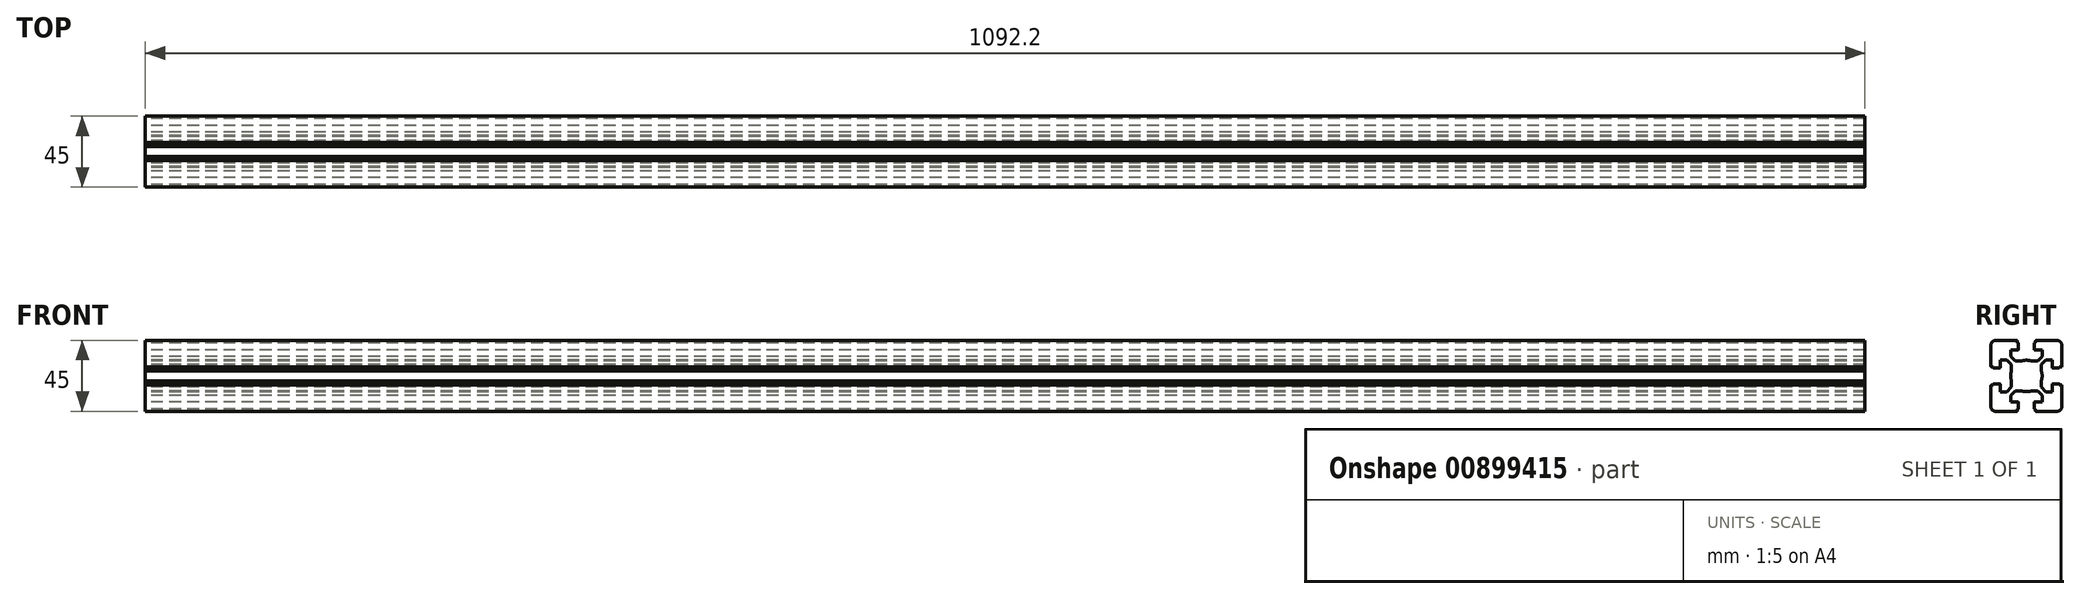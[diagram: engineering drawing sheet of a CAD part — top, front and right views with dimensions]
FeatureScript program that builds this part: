
annotation { "Feature Type Name" : "Feature", "Feature Type Description" : "" }
export const myFeature = defineFeature(function(context is Context, id is Id, definition is map)
    precondition{}
    {
        {
            var Q0;
            Q0=qCreatedBy(makeId("Right.planeOp"),FACE);
            var sketch = newSketch(context, id + "F0", { "sketchPlane" : qUnion([Q0])});
            skLineSegment(sketch, "E0", {"start": v(-20.09, -10.29) * mm, "end": v(-21.29, -10.29) * mm});
            skArc(sketch, "E1", {"start": v(-21.29, -10.29) * mm, "mid": v(-21.5, -10.38) * mm, "end": v(-21.59, -10.59) * mm});
            skLineSegment(sketch, "E2", {"start": v(-21.59, -10.59) * mm, "end": v(-21.59, -23.99) * mm});
            skArc(sketch, "E3", {"start": v(-21.59, -23.99) * mm, "mid": v(-20.7, -26.11) * mm, "end": v(-18.59, -26.99) * mm});
            skLineSegment(sketch, "E4", {"start": v(-18.59, -26.99) * mm, "end": v(-5.19, -26.99) * mm});
            skArc(sketch, "E5", {"start": v(-5.19, -26.99) * mm, "mid": v(-4.98, -26.9) * mm, "end": v(-4.89, -26.69) * mm});
            skLineSegment(sketch, "E6", {"start": v(-4.89, -26.69) * mm, "end": v(-4.89, -25.49) * mm});
            skLineSegment(sketch, "E7", {"start": v(-4.89, -25.49) * mm, "end": v(-4.39, -25.49) * mm});
            skArc(sketch, "E8", {"start": v(-4.39, -25.49) * mm, "mid": v(-4.18, -25.4) * mm, "end": v(-4.09, -25.19) * mm});
            skLineSegment(sketch, "E9", {"start": v(-4.09, -25.19) * mm, "end": v(-4.09, -21.29) * mm});
            skArc(sketch, "E10", {"start": v(-4.09, -21.29) * mm, "mid": v(-4.18, -21.08) * mm, "end": v(-4.39, -20.99) * mm});
            skLineSegment(sketch, "E11", {"start": v(-4.39, -20.99) * mm, "end": v(-9.14, -20.99) * mm});
            skLineSegment(sketch, "E12", {"start": v(-9.14, -20.99) * mm, "end": v(-9.14, -16.88) * mm});
            skLineSegment(sketch, "E13", {"start": v(-9.14, -16.88) * mm, "end": v(-6.25, -13.99) * mm});
            skLineSegment(sketch, "E14", {"start": v(-6.25, -13.99) * mm, "end": v(-2.21, -13.99) * mm});
            skArc(sketch, "E15", {"start": v(-2.21, -13.99) * mm, "mid": v(0.91, -14.49) * mm, "end": v(4.03, -13.99) * mm});
            skLineSegment(sketch, "E16", {"start": v(-20.09, -10.29) * mm, "end": v(-20.09, -9.79) * mm});
            skArc(sketch, "E17", {"start": v(-20.09, -9.79) * mm, "mid": v(-20, -9.58) * mm, "end": v(-19.79, -9.49) * mm});
            skLineSegment(sketch, "E18", {"start": v(-19.79, -9.49) * mm, "end": v(-15.89, -9.49) * mm});
            skArc(sketch, "E19", {"start": v(-15.89, -9.49) * mm, "mid": v(-15.68, -9.58) * mm, "end": v(-15.59, -9.79) * mm});
            skLineSegment(sketch, "E20", {"start": v(-15.59, -9.79) * mm, "end": v(-15.59, -14.54) * mm});
            skLineSegment(sketch, "E21", {"start": v(-15.59, -14.54) * mm, "end": v(-11.48, -14.54) * mm});
            skLineSegment(sketch, "E22", {"start": v(-11.48, -14.54) * mm, "end": v(-8.59, -11.65) * mm});
            skLineSegment(sketch, "E23", {"start": v(-8.59, -11.65) * mm, "end": v(-8.59, -7.61) * mm});
            skLineSegment(sketch, "E24", {"start": v(29.82, -4.49) * mm, "end": v(-31.05, -4.49) * mm});
            skLineSegment(sketch, "E25.MirrorCS", {"start": v(6.71, -25.49) * mm, "end": v(6.21, -25.49) * mm});
            skArc(sketch, "E26.MirrorCS", {"start": v(7.01, -26.99) * mm, "mid": v(6.8, -26.9) * mm, "end": v(6.71, -26.69) * mm});
            skLineSegment(sketch, "E27.MirrorCS", {"start": v(10.41, -11.65) * mm, "end": v(10.41, -7.61) * mm});
            skArc(sketch, "E28.MirrorCS", {"start": v(6.21, -25.49) * mm, "mid": v(6, -25.4) * mm, "end": v(5.91, -25.19) * mm});
            skLineSegment(sketch, "E29.MirrorCS", {"start": v(6.71, -26.69) * mm, "end": v(6.71, -25.49) * mm});
            skArc(sketch, "E30.MirrorCS", {"start": v(5.91, -21.29) * mm, "mid": v(6, -21.08) * mm, "end": v(6.21, -20.99) * mm});
            skLineSegment(sketch, "E31.MirrorCS", {"start": v(10.96, -16.88) * mm, "end": v(8.07, -13.99) * mm});
            skLineSegment(sketch, "E32.MirrorCS", {"start": v(13.3, -14.54) * mm, "end": v(10.41, -11.65) * mm});
            skLineSegment(sketch, "E33.MirrorCS", {"start": v(17.41, -14.54) * mm, "end": v(13.3, -14.54) * mm});
            skLineSegment(sketch, "E34.MirrorCS", {"start": v(17.41, -9.79) * mm, "end": v(17.41, -14.54) * mm});
            skLineSegment(sketch, "E35.MirrorCS", {"start": v(6.21, -20.99) * mm, "end": v(10.96, -20.99) * mm});
            skLineSegment(sketch, "E36.MirrorCS", {"start": v(8.07, -13.99) * mm, "end": v(4.03, -13.99) * mm});
            skArc(sketch, "E37.MirrorCS", {"start": v(4.03, -13.99) * mm, "mid": v(0.91, -14.49) * mm, "end": v(-2.21, -13.99) * mm});
            skLineSegment(sketch, "E38.MirrorCS", {"start": v(10.96, -20.99) * mm, "end": v(10.96, -16.88) * mm});
            skLineSegment(sketch, "E39.MirrorCS", {"start": v(5.91, -25.19) * mm, "end": v(5.91, -21.29) * mm});
            skArc(sketch, "E40.MirrorCS", {"start": v(23.41, -23.99) * mm, "mid": v(22.53, -26.11) * mm, "end": v(20.41, -26.99) * mm});
            skLineSegment(sketch, "E41.MirrorCS", {"start": v(20.41, -26.99) * mm, "end": v(7.01, -26.99) * mm});
            skLineSegment(sketch, "E42.MirrorCS", {"start": v(23.41, -10.59) * mm, "end": v(23.41, -23.99) * mm});
            skArc(sketch, "E43.MirrorCS", {"start": v(17.71, -9.49) * mm, "mid": v(17.5, -9.58) * mm, "end": v(17.41, -9.79) * mm});
            skArc(sketch, "E44.MirrorCS", {"start": v(23.11, -10.29) * mm, "mid": v(23.32, -10.38) * mm, "end": v(23.41, -10.59) * mm});
            skLineSegment(sketch, "E45.MirrorCS", {"start": v(21.91, -10.29) * mm, "end": v(21.91, -9.79) * mm});
            skLineSegment(sketch, "E46.MirrorCS", {"start": v(21.91, -10.29) * mm, "end": v(23.11, -10.29) * mm});
            skArc(sketch, "E47.MirrorCS", {"start": v(21.91, -9.79) * mm, "mid": v(21.82, -9.58) * mm, "end": v(21.61, -9.49) * mm});
            skLineSegment(sketch, "E48.MirrorCS", {"start": v(21.61, -9.49) * mm, "end": v(17.71, -9.49) * mm});
            skLineSegment(sketch, "E49.MirrorCS", {"start": v(6.71, 16.51) * mm, "end": v(6.21, 16.51) * mm});
            skArc(sketch, "E50.MirrorCS", {"start": v(-4.39, 16.51) * mm, "mid": v(-4.18, 16.42) * mm, "end": v(-4.09, 16.21) * mm});
            skLineSegment(sketch, "E51.MirrorCS", {"start": v(-4.89, 16.51) * mm, "end": v(-4.39, 16.51) * mm});
            skArc(sketch, "E52.MirrorCS", {"start": v(5.91, 12.31) * mm, "mid": v(6, 12.1) * mm, "end": v(6.21, 12.01) * mm});
            skLineSegment(sketch, "E53.MirrorCS", {"start": v(6.71, 17.71) * mm, "end": v(6.71, 16.51) * mm});
            skLineSegment(sketch, "E54.MirrorCS", {"start": v(-4.89, 17.71) * mm, "end": v(-4.89, 16.51) * mm});
            skArc(sketch, "E55.MirrorCS", {"start": v(-5.19, 18.01) * mm, "mid": v(-4.98, 17.92) * mm, "end": v(-4.89, 17.71) * mm});
            skArc(sketch, "E56.MirrorCS", {"start": v(-4.09, 12.31) * mm, "mid": v(-4.18, 12.1) * mm, "end": v(-4.39, 12.01) * mm});
            skArc(sketch, "E57.MirrorCS", {"start": v(7.01, 18.01) * mm, "mid": v(6.8, 17.92) * mm, "end": v(6.71, 17.71) * mm});
            skArc(sketch, "E58.MirrorCS", {"start": v(6.21, 16.51) * mm, "mid": v(6, 16.42) * mm, "end": v(5.91, 16.21) * mm});
            skArc(sketch, "E59.MirrorCS", {"start": v(23.11, 1.31) * mm, "mid": v(23.32, 1.4) * mm, "end": v(23.41, 1.61) * mm});
            skLineSegment(sketch, "E60.MirrorCS", {"start": v(21.91, 1.31) * mm, "end": v(21.91, 0.81) * mm});
            skArc(sketch, "E61.MirrorCS", {"start": v(-15.89, 0.51) * mm, "mid": v(-15.68, 0.6) * mm, "end": v(-15.59, 0.81) * mm});
            skArc(sketch, "E62.MirrorCS", {"start": v(-21.29, 1.31) * mm, "mid": v(-21.5, 1.4) * mm, "end": v(-21.59, 1.61) * mm});
            skArc(sketch, "E63.MirrorCS", {"start": v(17.71, 0.51) * mm, "mid": v(17.5, 0.6) * mm, "end": v(17.41, 0.81) * mm});
            skArc(sketch, "E64.MirrorCS", {"start": v(21.91, 0.81) * mm, "mid": v(21.82, 0.6) * mm, "end": v(21.61, 0.51) * mm});
            skLineSegment(sketch, "E65.MirrorCS", {"start": v(21.91, 1.31) * mm, "end": v(23.11, 1.31) * mm});
            skArc(sketch, "E66.MirrorCS", {"start": v(14.31, 5.31) * mm, "mid": v(14.1, 5.4) * mm, "end": v(14.01, 5.61) * mm});
            skArc(sketch, "E67.MirrorCS", {"start": v(-20.09, 0.81) * mm, "mid": v(-20, 0.6) * mm, "end": v(-19.79, 0.51) * mm});
            skLineSegment(sketch, "E68.MirrorCS", {"start": v(-20.09, 1.31) * mm, "end": v(-21.29, 1.31) * mm});
            skLineSegment(sketch, "E69.MirrorCS", {"start": v(-20.09, 1.31) * mm, "end": v(-20.09, 0.81) * mm});
            skLineSegment(sketch, "E70.MirrorCS", {"start": v(8.07, 5.01) * mm, "end": v(4.03, 5.01) * mm});
            skLineSegment(sketch, "E71.MirrorCS", {"start": v(-4.09, 16.21) * mm, "end": v(-4.09, 12.31) * mm});
            skLineSegment(sketch, "E72.MirrorCS", {"start": v(-9.14, 12.01) * mm, "end": v(-9.14, 7.9) * mm});
            skLineSegment(sketch, "E73.MirrorCS", {"start": v(-15.59, 5.56) * mm, "end": v(-11.48, 5.56) * mm});
            skLineSegment(sketch, "E74.MirrorCS", {"start": v(-4.39, 12.01) * mm, "end": v(-9.14, 12.01) * mm});
            skLineSegment(sketch, "E75.MirrorCS", {"start": v(-9.14, 7.9) * mm, "end": v(-6.25, 5.01) * mm});
            skLineSegment(sketch, "E76.MirrorCS", {"start": v(10.96, 12.01) * mm, "end": v(10.96, 7.9) * mm});
            skArc(sketch, "E77.MirrorCS", {"start": v(-21.59, 15.01) * mm, "mid": v(-20.7, 17.13) * mm, "end": v(-18.59, 18.01) * mm});
            skLineSegment(sketch, "E78.MirrorCS", {"start": v(23.41, 1.61) * mm, "end": v(23.41, 15.01) * mm});
            skLineSegment(sketch, "E79.MirrorCS", {"start": v(13.3, 5.56) * mm, "end": v(10.41, 2.67) * mm});
            skLineSegment(sketch, "E80.MirrorCS", {"start": v(-8.59, 2.67) * mm, "end": v(-8.59, -1.37) * mm});
            skLineSegment(sketch, "E81.MirrorCS", {"start": v(-15.59, 0.81) * mm, "end": v(-15.59, 5.56) * mm});
            skLineSegment(sketch, "E82.MirrorCS", {"start": v(10.41, 2.67) * mm, "end": v(10.41, -1.37) * mm});
            skLineSegment(sketch, "E83.MirrorCS", {"start": v(-18.59, 18.01) * mm, "end": v(-5.19, 18.01) * mm});
            skLineSegment(sketch, "E84.MirrorCS", {"start": v(10.96, 7.9) * mm, "end": v(8.07, 5.01) * mm});
            skLineSegment(sketch, "E85.MirrorCS", {"start": v(17.41, 5.56) * mm, "end": v(13.3, 5.56) * mm});
            skArc(sketch, "E86.MirrorCS", {"start": v(23.41, 15.01) * mm, "mid": v(22.53, 17.13) * mm, "end": v(20.41, 18.01) * mm});
            skLineSegment(sketch, "E87.MirrorCS", {"start": v(5.91, 16.21) * mm, "end": v(5.91, 12.31) * mm});
            skLineSegment(sketch, "E88.MirrorCS", {"start": v(17.41, 0.81) * mm, "end": v(17.41, 5.56) * mm});
            skLineSegment(sketch, "E89.MirrorCS", {"start": v(-11.48, 5.56) * mm, "end": v(-8.59, 2.67) * mm});
            skLineSegment(sketch, "E90.MirrorCS", {"start": v(-6.25, 5.01) * mm, "end": v(-2.21, 5.01) * mm});
            skLineSegment(sketch, "E91.MirrorCS", {"start": v(-21.59, 1.61) * mm, "end": v(-21.59, 15.01) * mm});
            skArc(sketch, "E92.MirrorCS", {"start": v(4.03, 5.01) * mm, "mid": v(0.91, 5.51) * mm, "end": v(-2.21, 5.01) * mm});
            skLineSegment(sketch, "E93.MirrorCS", {"start": v(6.21, 12.01) * mm, "end": v(10.96, 12.01) * mm});
            skArc(sketch, "E94.MirrorCS", {"start": v(-2.21, 5.01) * mm, "mid": v(0.91, 5.51) * mm, "end": v(4.03, 5.01) * mm});
            skLineSegment(sketch, "E95.MirrorCS", {"start": v(20.41, 18.01) * mm, "end": v(7.01, 18.01) * mm});
            skLineSegment(sketch, "E96.MirrorCS", {"start": v(-19.79, 0.51) * mm, "end": v(-15.89, 0.51) * mm});
            skLineSegment(sketch, "E97.MirrorCS", {"start": v(21.61, 0.51) * mm, "end": v(17.71, 0.51) * mm});
            skLineSegment(sketch, "E98.MirrorCS", {"start": v(0.91, -27.65) * mm, "end": v(0.91, 19.82) * mm});
            skArc(sketch, "E99", {"start": v(-8.59, -1.37) * mm, "mid": v(-9.09, -4.49) * mm, "end": v(-8.59, -7.61) * mm});
            skArc(sketch, "E100", {"start": v(10.41, -7.61) * mm, "mid": v(10.91, -4.49) * mm, "end": v(10.41, -1.37) * mm});
            skSolve(sketch);
        }
        {
            var Q0;
            Q0=qSketchRegion(id+"F0",true);
            extrude(context, id + "F1", {"entities" : qUnion([Q0]), "depth" : 1092.2 * mm, "offsetDistance" : 25.4 * mm});
        }
    });
